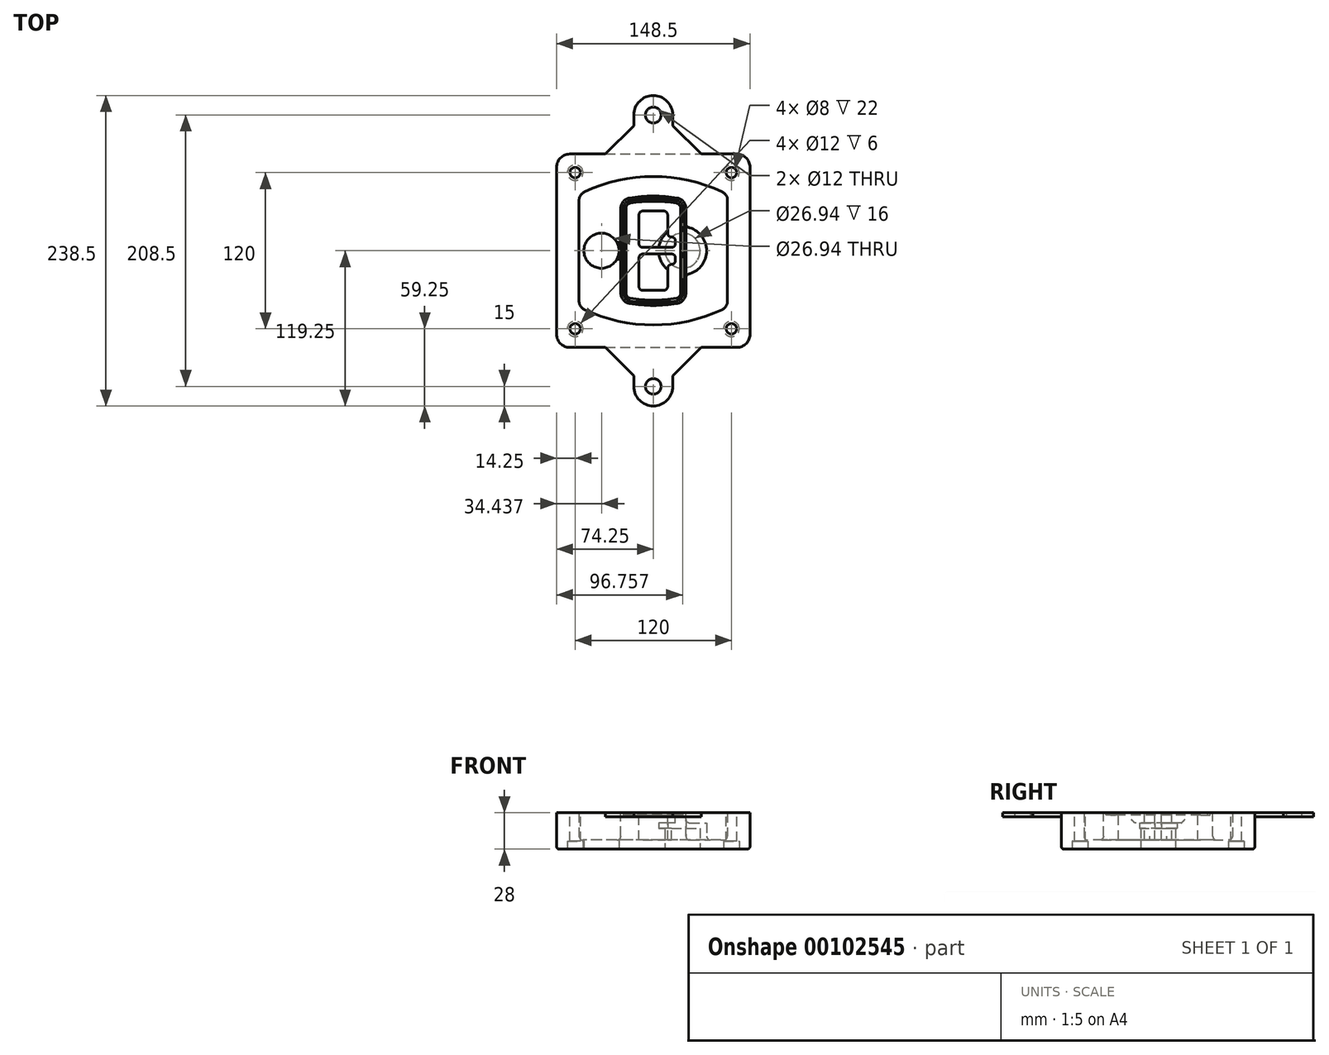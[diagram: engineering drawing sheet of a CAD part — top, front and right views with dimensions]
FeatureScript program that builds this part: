
annotation { "Feature Type Name" : "Feature", "Feature Type Description" : "" }
export const myFeature = defineFeature(function(context is Context, id is Id, definition is map)
    precondition{}
    {
        {
            var Q0;
            Q0=qCreatedBy(makeId("Top.planeOp"),FACE);
            var sketch = newSketch(context, id + "F0", { "sketchPlane" : qUnion([Q0])});
            skPoint(sketch, "E0.rect.middle", {"position": v(0, 0) * mm});
            skLineSegment(sketch, "E1.bottom", {"start": v(-64.25, -74.25) * mm, "end": v(64.25, -74.25) * mm});
            skLineSegment(sketch, "E1.top", {"start": v(-64.25, 74.25) * mm, "end": v(64.25, 74.25) * mm});
            skLineSegment(sketch, "E1.left", {"start": v(-74.25, -64.25) * mm, "end": v(-74.25, 64.25) * mm});
            skLineSegment(sketch, "E1.right", {"start": v(74.25, -64.25) * mm, "end": v(74.25, 64.25) * mm});
            skLineSegment(sketch, "E2", {"start": v(-74.25, 74.25) * mm, "end": v(74.25, -74.25) * mm, "construction": true});
            skLineSegment(sketch, "E3", {"start": v(74.25, 74.25) * mm, "end": v(-74.25, -74.25) * mm, "construction": true});
            skCircle(sketch, "E4", {"center": v(-60, 60) * mm, "radius": 4 * mm});
            skCircle(sketch, "E5", {"center": v(60, 60) * mm, "radius": 4 * mm});
            skCircle(sketch, "E6", {"center": v(60, -60) * mm, "radius": 4 * mm});
            skCircle(sketch, "E7", {"center": v(-60, -60) * mm, "radius": 4 * mm});
            skLineSegment(sketch, "E8", {"start": v(-60, 60) * mm, "end": v(60, 60) * mm, "construction": true});
            skLineSegment(sketch, "E9", {"start": v(60, 60) * mm, "end": v(60, -60) * mm, "construction": true});
            skLineSegment(sketch, "E10", {"start": v(60, -60) * mm, "end": v(-60, -60) * mm, "construction": true});
            skLineSegment(sketch, "E11", {"start": v(-60, -60) * mm, "end": v(-60, 60) * mm, "construction": true});
            skLineSegment(sketch, "E12", {"start": v(-60, 38.83) * mm, "end": v(-60, -38.83) * mm});
            skLineSegment(sketch, "E13", {"start": v(60, 38.83) * mm, "end": v(60, -38.83) * mm});
            skArc(sketch, "E14", {"start": v(54.26, 47.88) * mm, "mid": v(0, 60) * mm, "end": v(-54.26, 47.88) * mm});
            skArc(sketch, "E15", {"start": v(-54.26, -47.88) * mm, "mid": v(0, -60) * mm, "end": v(54.26, -47.88) * mm});
            skLineSegment(sketch, "E16", {"start": v(-60, 0) * mm, "end": v(60, 0) * mm, "construction": true});
            skPoint(sketch, "E17.visualSharp", {"position": v(-60, -45) * mm});
            skArc(sketch, "E17.filletArc", {"start": v(-60, -38.83) * mm, "mid": v(-58.44, -44.2) * mm, "end": v(-54.26, -47.88) * mm});
            skPoint(sketch, "E18.visualSharp", {"position": v(-60, 45) * mm});
            skArc(sketch, "E18.filletArc", {"start": v(-54.26, 47.88) * mm, "mid": v(-58.44, 44.2) * mm, "end": v(-60, 38.83) * mm});
            skPoint(sketch, "E19.visualSharp", {"position": v(60, 45) * mm});
            skArc(sketch, "E19.filletArc", {"start": v(60, 38.83) * mm, "mid": v(58.44, 44.2) * mm, "end": v(54.26, 47.88) * mm});
            skPoint(sketch, "E20.visualSharp", {"position": v(60, -45) * mm});
            skArc(sketch, "E20.filletArc", {"start": v(54.26, -47.88) * mm, "mid": v(58.44, -44.2) * mm, "end": v(60, -38.83) * mm});
            skPoint(sketch, "E21.visualSharp", {"position": v(-74.25, 74.25) * mm});
            skArc(sketch, "E21.filletArc", {"start": v(-64.25, 74.25) * mm, "mid": v(-71.32, 71.32) * mm, "end": v(-74.25, 64.25) * mm});
            skPoint(sketch, "E22.visualSharp", {"position": v(74.25, 74.25) * mm});
            skArc(sketch, "E22.filletArc", {"start": v(74.25, 64.25) * mm, "mid": v(71.32, 71.32) * mm, "end": v(64.25, 74.25) * mm});
            skPoint(sketch, "E23.visualSharp", {"position": v(74.25, -74.25) * mm});
            skArc(sketch, "E23.filletArc", {"start": v(64.25, -74.25) * mm, "mid": v(71.32, -71.32) * mm, "end": v(74.25, -64.25) * mm});
            skPoint(sketch, "E24.visualSharp", {"position": v(-74.25, -74.25) * mm});
            skArc(sketch, "E24.filletArc", {"start": v(-74.25, -64.25) * mm, "mid": v(-71.32, -71.32) * mm, "end": v(-64.25, -74.25) * mm});
            skArc(sketch, "E25.0", {"start": v(57, 38.83) * mm, "mid": v(55.9, 42.58) * mm, "end": v(52.98, 45.17) * mm});
            skLineSegment(sketch, "E25.1", {"start": v(57, 38.83) * mm, "end": v(57, -38.83) * mm});
            skArc(sketch, "E25.2", {"start": v(52.98, -45.17) * mm, "mid": v(55.9, -42.58) * mm, "end": v(57, -38.83) * mm});
            skArc(sketch, "E25.3", {"start": v(-52.98, -45.17) * mm, "mid": v(0, -57) * mm, "end": v(52.98, -45.17) * mm});
            skArc(sketch, "E25.4", {"start": v(-57, -38.83) * mm, "mid": v(-55.9, -42.58) * mm, "end": v(-52.98, -45.17) * mm});
            skArc(sketch, "E25.5", {"start": v(52.98, 45.17) * mm, "mid": v(0, 57) * mm, "end": v(-52.98, 45.17) * mm});
            skLineSegment(sketch, "E25.6", {"start": v(-57, 38.83) * mm, "end": v(-57, -38.83) * mm});
            skArc(sketch, "E25.7", {"start": v(-52.98, 45.17) * mm, "mid": v(-55.9, 42.58) * mm, "end": v(-57, 38.83) * mm});
            skArc(sketch, "E26.0", {"start": v(-55.96, 51.5) * mm, "mid": v(-61.82, 46.33) * mm, "end": v(-64, 38.83) * mm});
            skArc(sketch, "E26.1", {"start": v(55.96, 51.5) * mm, "mid": v(0, 64) * mm, "end": v(-55.96, 51.5) * mm});
            skArc(sketch, "E26.2", {"start": v(64, 38.83) * mm, "mid": v(61.82, 46.33) * mm, "end": v(55.96, 51.5) * mm});
            skLineSegment(sketch, "E26.3", {"start": v(64, 38.83) * mm, "end": v(64, -38.83) * mm});
            skArc(sketch, "E26.4", {"start": v(55.96, -51.5) * mm, "mid": v(61.82, -46.33) * mm, "end": v(64, -38.83) * mm});
            skLineSegment(sketch, "E26.5", {"start": v(-64, 38.83) * mm, "end": v(-64, -38.83) * mm});
            skArc(sketch, "E26.6", {"start": v(-55.96, -51.5) * mm, "mid": v(0, -64) * mm, "end": v(55.96, -51.5) * mm});
            skArc(sketch, "E26.7", {"start": v(-64, -38.83) * mm, "mid": v(-61.82, -46.33) * mm, "end": v(-55.96, -51.5) * mm});
            skSolve(sketch);
        }
        {
            var Q0;
            Q0=makeQuery(id+"F0.imprint","IMPRINT",FACE,{"disambiguationData":[TD([[makeQuery(id+"F0.imprint","IMPRINT",EDGE,{"derivedFrom":sQuery(id+"F0.wireOp",EDGE,"E1.bottom")}),1.0]])]});
            var Q1;
            Q1=makeQuery(id+"F0.imprint","IMPRINT",FACE,{"disambiguationData":[TD([[makeQuery(id+"F0.imprint","IMPRINT",EDGE,{"derivedFrom":sQuery(id+"F0.wireOp",EDGE,"E12")}),1.0]])]});
            var Q2;
            Q2=makeQuery(id+"F0.imprint","IMPRINT",FACE,{"disambiguationData":[TD([[makeQuery(id+"F0.imprint","IMPRINT",EDGE,{"derivedFrom":sQuery(id+"F0.wireOp",EDGE,"E25.0")}),1.0]])]});
            var Q3;
            Q3=makeQuery(id+"F0.imprint","IMPRINT",FACE,{"disambiguationData":[TD([[makeQuery(id+"F0.imprint","IMPRINT",EDGE,{"derivedFrom":sQuery(id+"F0.wireOp",EDGE,"E12")}),-1.0]])]});
            extrude(context, id + "F1", {"entities" : qUnion([Q0, Q1, Q2, Q3]), "oppositeDirection" : true, "depth" : 25 * mm});
        }
        {
            var Q0;
            Q0=makeQuery(id+"F0.imprint","IMPRINT",FACE,{"disambiguationData":[TD([[makeQuery(id+"F0.imprint","IMPRINT",EDGE,{"derivedFrom":sQuery(id+"F0.wireOp",EDGE,"E12")}),1.0]])]});
            extrude(context, id + "F2", {"entities" : qUnion([Q0]), "operationType" : NewBodyOperationType.ADD, "depth" : 3 * mm});
        }
        {
            var Q0;
            Q0=makeQuery(id+"F0.imprint","IMPRINT",FACE,{"disambiguationData":[TD([[makeQuery(id+"F0.imprint","IMPRINT",EDGE,{"derivedFrom":sQuery(id+"F0.wireOp",EDGE,"E25.0")}),1.0]])]});
            extrude(context, id + "F3", {"entities" : qUnion([Q0]), "operationType" : NewBodyOperationType.REMOVE, "oppositeDirection" : true, "depth" : 18 * mm});
        }
        {
            var Q0;
            Q0=makeQuery(id+"F2.opExtrude","CAP_FACE",FACE,{"disambiguationData":[OSD([sQuery(id+"F0.wireOp",EDGE,"E12"),sQuery(id+"F0.wireOp",EDGE,"E13"),sQuery(id+"F0.wireOp",EDGE,"E14"),sQuery(id+"F0.wireOp",EDGE,"E15"),sQuery(id+"F0.wireOp",EDGE,"E17.filletArc"),sQuery(id+"F0.wireOp",EDGE,"E18.filletArc"),sQuery(id+"F0.wireOp",EDGE,"E19.filletArc"),sQuery(id+"F0.wireOp",EDGE,"E20.filletArc"),sQuery(id+"F0.wireOp",EDGE,"E25.0"),sQuery(id+"F0.wireOp",EDGE,"E25.1"),sQuery(id+"F0.wireOp",EDGE,"E25.2"),sQuery(id+"F0.wireOp",EDGE,"E25.3"),sQuery(id+"F0.wireOp",EDGE,"E25.4"),sQuery(id+"F0.wireOp",EDGE,"E25.5"),sQuery(id+"F0.wireOp",EDGE,"E25.6"),sQuery(id+"F0.wireOp",EDGE,"E25.7")])],"isStart":false});
            var sketch = newSketch(context, id + "F4", { "sketchPlane" : qUnion([Q0])});
            skArc(sketch, "E27.0", {"start": v(-18.34, -40.45) * mm, "mid": v(0, -42) * mm, "end": v(18.34, -40.45) * mm});
            skArc(sketch, "E28.0", {"start": v(18.34, 40.45) * mm, "mid": v(0, 42) * mm, "end": v(-18.34, 40.45) * mm});
            skLineSegment(sketch, "E29", {"start": v(-25, 32.57) * mm, "end": v(-25, -32.57) * mm});
            skLineSegment(sketch, "E30", {"start": v(25, 32.57) * mm, "end": v(25, -32.57) * mm});
            skLineSegment(sketch, "E31", {"start": v(-25, 39.1) * mm, "end": v(25, 39.1) * mm, "construction": true});
            skLineSegment(sketch, "E32", {"start": v(-25, -39.1) * mm, "end": v(25, -39.1) * mm, "construction": true});
            skPoint(sketch, "E33.visualSharp", {"position": v(-25, 39.1) * mm});
            skArc(sketch, "E33.filletArc", {"start": v(-18.34, 40.45) * mm, "mid": v(-23.11, 37.73) * mm, "end": v(-25, 32.57) * mm});
            skPoint(sketch, "E34.visualSharp", {"position": v(25, 39.1) * mm});
            skArc(sketch, "E34.filletArc", {"start": v(25, 32.57) * mm, "mid": v(23.11, 37.73) * mm, "end": v(18.34, 40.45) * mm});
            skPoint(sketch, "E35.visualSharp", {"position": v(25, -39.1) * mm});
            skArc(sketch, "E35.filletArc", {"start": v(18.34, -40.45) * mm, "mid": v(23.11, -37.73) * mm, "end": v(25, -32.57) * mm});
            skPoint(sketch, "E36.visualSharp", {"position": v(-25, -39.1) * mm});
            skArc(sketch, "E36.filletArc", {"start": v(-25, -32.57) * mm, "mid": v(-23.11, -37.73) * mm, "end": v(-18.34, -40.45) * mm});
            skArc(sketch, "E37.0", {"start": v(52.98, 45.17) * mm, "mid": v(0, 57) * mm, "end": v(-52.98, 45.17) * mm});
            skArc(sketch, "E37.1", {"start": v(-52.98, 45.17) * mm, "mid": v(-55.9, 42.58) * mm, "end": v(-57, 38.83) * mm});
            skLineSegment(sketch, "E37.2", {"start": v(-57, 38.83) * mm, "end": v(-57, -38.83) * mm});
            skArc(sketch, "E37.3", {"start": v(-57, -38.83) * mm, "mid": v(-55.9, -42.58) * mm, "end": v(-52.98, -45.17) * mm});
            skArc(sketch, "E37.4", {"start": v(-52.98, -45.17) * mm, "mid": v(0, -57) * mm, "end": v(52.98, -45.17) * mm});
            skArc(sketch, "E37.5", {"start": v(52.98, -45.17) * mm, "mid": v(55.9, -42.58) * mm, "end": v(57, -38.83) * mm});
            skLineSegment(sketch, "E37.6", {"start": v(57, 38.83) * mm, "end": v(57, -38.83) * mm});
            skArc(sketch, "E37.7", {"start": v(57, 38.83) * mm, "mid": v(55.9, 42.58) * mm, "end": v(52.98, 45.17) * mm});
            skLineSegment(sketch, "E38.0", {"start": v(23, 32.57) * mm, "end": v(23, -32.57) * mm});
            skArc(sketch, "E38.1", {"start": v(18, -38.48) * mm, "mid": v(21.58, -36.44) * mm, "end": v(23, -32.57) * mm});
            skArc(sketch, "E38.2", {"start": v(-18, -38.48) * mm, "mid": v(0, -40) * mm, "end": v(18, -38.48) * mm});
            skArc(sketch, "E38.3", {"start": v(-23, -32.57) * mm, "mid": v(-21.58, -36.44) * mm, "end": v(-18, -38.48) * mm});
            skLineSegment(sketch, "E38.4", {"start": v(-23, 32.57) * mm, "end": v(-23, -32.57) * mm});
            skArc(sketch, "E38.5", {"start": v(23, 32.57) * mm, "mid": v(21.58, 36.44) * mm, "end": v(18, 38.48) * mm});
            skArc(sketch, "E38.6", {"start": v(-18, 38.48) * mm, "mid": v(-21.58, 36.44) * mm, "end": v(-23, 32.57) * mm});
            skArc(sketch, "E38.7", {"start": v(18, 38.48) * mm, "mid": v(0, 40) * mm, "end": v(-18, 38.48) * mm});
            skArc(sketch, "E39.0", {"start": v(21, 32.57) * mm, "mid": v(20.06, 35.15) * mm, "end": v(17.67, 36.5) * mm});
            skLineSegment(sketch, "E39.1", {"start": v(21, 32.57) * mm, "end": v(21, -32.57) * mm});
            skArc(sketch, "E39.2", {"start": v(17.67, -36.5) * mm, "mid": v(20.06, -35.15) * mm, "end": v(21, -32.57) * mm});
            skArc(sketch, "E39.3", {"start": v(-17.67, -36.5) * mm, "mid": v(0, -38) * mm, "end": v(17.67, -36.5) * mm});
            skArc(sketch, "E39.4", {"start": v(-21, -32.57) * mm, "mid": v(-20.06, -35.15) * mm, "end": v(-17.67, -36.5) * mm});
            skArc(sketch, "E39.5", {"start": v(17.67, 36.5) * mm, "mid": v(0, 38) * mm, "end": v(-17.67, 36.5) * mm});
            skLineSegment(sketch, "E39.6", {"start": v(-21, 32.57) * mm, "end": v(-21, -32.57) * mm});
            skArc(sketch, "E39.7", {"start": v(-17.67, 36.5) * mm, "mid": v(-20.06, 35.15) * mm, "end": v(-21, 32.57) * mm});
            skLineSegment(sketch, "E40", {"start": v(-25, 0) * mm, "end": v(25, 0) * mm, "construction": true});
            skLineSegment(sketch, "E41", {"start": v(-11, 5.5) * mm, "end": v(-11, 27.5) * mm});
            skLineSegment(sketch, "E42", {"start": v(-8, 30.5) * mm, "end": v(8, 30.5) * mm});
            skLineSegment(sketch, "E43", {"start": v(11, 27.5) * mm, "end": v(11, 13.5) * mm});
            skLineSegment(sketch, "E44", {"start": v(14, 10.5) * mm, "end": v(14, 10.5) * mm});
            skLineSegment(sketch, "E45", {"start": v(17, 7.5) * mm, "end": v(17, 5.5) * mm});
            skLineSegment(sketch, "E46", {"start": v(14, 2.5) * mm, "end": v(-8, 2.5) * mm});
            skPoint(sketch, "E47.visualSharp", {"position": v(-11, 30.5) * mm});
            skArc(sketch, "E47.filletArc", {"start": v(-8, 30.5) * mm, "mid": v(-10.12, 29.62) * mm, "end": v(-11, 27.5) * mm});
            skPoint(sketch, "E48.visualSharp", {"position": v(11, 30.5) * mm});
            skArc(sketch, "E48.filletArc", {"start": v(11, 27.5) * mm, "mid": v(10.12, 29.62) * mm, "end": v(8, 30.5) * mm});
            skPoint(sketch, "E49.visualSharp", {"position": v(11, 10.5) * mm});
            skArc(sketch, "E49.filletArc", {"start": v(11, 13.5) * mm, "mid": v(11.88, 11.38) * mm, "end": v(14, 10.5) * mm});
            skPoint(sketch, "E50.visualSharp", {"position": v(17, 10.5) * mm});
            skArc(sketch, "E50.filletArc", {"start": v(17, 7.5) * mm, "mid": v(16.12, 9.62) * mm, "end": v(14, 10.5) * mm});
            skPoint(sketch, "E51.visualSharp", {"position": v(17, 2.5) * mm});
            skArc(sketch, "E51.filletArc", {"start": v(14, 2.5) * mm, "mid": v(16.12, 3.38) * mm, "end": v(17, 5.5) * mm});
            skPoint(sketch, "E52.visualSharp", {"position": v(-11, 2.5) * mm});
            skArc(sketch, "E52.filletArc", {"start": v(-11, 5.5) * mm, "mid": v(-10.12, 3.38) * mm, "end": v(-8, 2.5) * mm});
            skLineSegment(sketch, "E53.0.MirrorCS", {"start": v(14, -2.5) * mm, "end": v(-8, -2.5) * mm});
            skArc(sketch, "E54.0.MirrorCS", {"start": v(-11, -5.5) * mm, "mid": v(-10.12, -3.38) * mm, "end": v(-8, -2.5) * mm});
            skLineSegment(sketch, "E55.0.MirrorCS", {"start": v(-11, -5.5) * mm, "end": v(-11, -27.5) * mm});
            skArc(sketch, "E56.0.MirrorCS", {"start": v(-8, -30.5) * mm, "mid": v(-10.12, -29.62) * mm, "end": v(-11, -27.5) * mm});
            skLineSegment(sketch, "E57.0.MirrorCS", {"start": v(-8, -30.5) * mm, "end": v(8, -30.5) * mm});
            skArc(sketch, "E58.0.MirrorCS", {"start": v(11, -27.5) * mm, "mid": v(10.12, -29.62) * mm, "end": v(8, -30.5) * mm});
            skLineSegment(sketch, "E59.0.MirrorCS", {"start": v(11, -27.5) * mm, "end": v(11, -13.5) * mm});
            skArc(sketch, "E60.0.MirrorCS", {"start": v(11, -13.5) * mm, "mid": v(11.88, -11.38) * mm, "end": v(14, -10.5) * mm});
            skArc(sketch, "E61.0.MirrorCS", {"start": v(17, -7.5) * mm, "mid": v(16.12, -9.62) * mm, "end": v(14, -10.5) * mm});
            skLineSegment(sketch, "E62.0.MirrorCS", {"start": v(17, -7.5) * mm, "end": v(17, -5.5) * mm});
            skArc(sketch, "E63.0.MirrorCS", {"start": v(14, -2.5) * mm, "mid": v(16.12, -3.38) * mm, "end": v(17, -5.5) * mm});
            skSolve(sketch);
        }
        {
            var Q0;
            Q0=makeQuery(id+"F4.imprint","IMPRINT",FACE,{"disambiguationData":[TD([[makeQuery(id+"F4.imprint","IMPRINT",EDGE,{"derivedFrom":sQuery(id+"F4.wireOp",EDGE,"E27.0")}),1.0]])]});
            var Q1;
            Q1=makeQuery(id+"F4.imprint","IMPRINT",FACE,{"disambiguationData":[TD([[makeQuery(id+"F4.imprint","IMPRINT",EDGE,{"derivedFrom":sQuery(id+"F4.wireOp",EDGE,"E38.0")}),-1.0]])]});
            var Q2;
            Q2=makeQuery(id+"F4.imprint","IMPRINT",FACE,{"disambiguationData":[TD([[makeQuery(id+"F4.imprint","IMPRINT",EDGE,{"derivedFrom":sQuery(id+"F4.wireOp",EDGE,"E39.0")}),1.0]])]});
            extrude(context, id + "F5", {"entities" : qUnion([Q0, Q1, Q2]), "operationType" : NewBodyOperationType.ADD, "endBound" : BoundingType.UP_TO_NEXT, "oppositeDirection" : true, "depth" : 25 * mm});
        }
        {
            var Q0;
            Q0=makeQuery(id+"F4.imprint","IMPRINT",FACE,{"disambiguationData":[TD([[makeQuery(id+"F4.imprint","IMPRINT",EDGE,{"derivedFrom":sQuery(id+"F4.wireOp",EDGE,"E38.0")}),-1.0]])]});
            extrude(context, id + "F6", {"entities" : qUnion([Q0]), "operationType" : NewBodyOperationType.REMOVE, "oppositeDirection" : true, "depth" : 2 * mm});
        }
        {
            var Q0;
            Q0=makeQuery(id+"F1.opExtrude","CAP_FACE",FACE,{"disambiguationData":[OSD([sQuery(id+"F0.wireOp",EDGE,"E1.bottom"),sQuery(id+"F0.wireOp",EDGE,"E1.top"),sQuery(id+"F0.wireOp",EDGE,"E1.left"),sQuery(id+"F0.wireOp",EDGE,"E1.right"),sQuery(id+"F0.wireOp",EDGE,"E4"),sQuery(id+"F0.wireOp",EDGE,"E5"),sQuery(id+"F0.wireOp",EDGE,"E6"),sQuery(id+"F0.wireOp",EDGE,"E7"),sQuery(id+"F0.wireOp",EDGE,"E21.filletArc"),sQuery(id+"F0.wireOp",EDGE,"E22.filletArc"),sQuery(id+"F0.wireOp",EDGE,"E23.filletArc"),sQuery(id+"F0.wireOp",EDGE,"E24.filletArc")])],"isStart":false});
            var sketch = newSketch(context, id + "F7", { "sketchPlane" : qUnion([Q0])});
            skCircle(sketch, "E64", {"center": v(22.5, 0) * mm, "radius": 13.47 * mm});
            skCircle(sketch, "E65", {"center": v(-39.81, 0) * mm, "radius": 13.47 * mm});
            skLineSegment(sketch, "E66", {"start": v(74.25, 0) * mm, "end": v(-74.25, 0) * mm});
            skCircle(sketch, "E67", {"center": v(22.5, 0) * mm, "radius": 18.47 * mm});
            skCircle(sketch, "E68", {"center": v(60, -60) * mm, "radius": 6 * mm});
            skCircle(sketch, "E69", {"center": v(-60, -60) * mm, "radius": 6 * mm});
            skCircle(sketch, "E70", {"center": v(-60, 60) * mm, "radius": 6 * mm});
            skCircle(sketch, "E71", {"center": v(60, 60) * mm, "radius": 6 * mm});
            skSolve(sketch);
        }
        {
            var Q0;
            {var subQ1=sQuery(id+"F7.wireOp",EDGE,"E66");var subQ4=sQuery(id+"F7.wireOp",EDGE,"E64");var subQ6=makeQuery(id+"F7.imprint","INTERSECT",VERTEX,{"disambiguationData":[OD(0.0)],"derivedFrom":[subQ4,subQ1]});Q0=makeQuery(id+"F7.imprint","IMPRINT",FACE,{"disambiguationData":[TD([[makeQuery(id+"F7.imprint","IMPRINT",EDGE,{"disambiguationData":[TD([[subQ6,-1.0]])],"derivedFrom":subQ4}),-1.0]])]});}
            var Q1;
            {var subQ0=sQuery(id+"F7.wireOp",EDGE,"E66");var subQ1=sQuery(id+"F7.wireOp",EDGE,"E64");var subQ3=makeQuery(id+"F7.imprint","INTERSECT",VERTEX,{"disambiguationData":[OD(0.0)],"derivedFrom":[subQ1,subQ0]});Q1=makeQuery(id+"F7.imprint","IMPRINT",FACE,{"disambiguationData":[TD([[makeQuery(id+"F7.imprint","IMPRINT",EDGE,{"disambiguationData":[TD([[subQ3,-1.0]])],"derivedFrom":subQ1}),1.0]])]});}
            var Q2;
            {var subQ0=sQuery(id+"F7.wireOp",EDGE,"E66");var subQ1=sQuery(id+"F7.wireOp",EDGE,"E64");var subQ3=makeQuery(id+"F7.imprint","INTERSECT",VERTEX,{"disambiguationData":[OD(0.0)],"derivedFrom":[subQ1,subQ0]});Q2=makeQuery(id+"F7.imprint","IMPRINT",FACE,{"disambiguationData":[TD([[makeQuery(id+"F7.imprint","IMPRINT",EDGE,{"disambiguationData":[TD([[subQ3,1.0]])],"derivedFrom":subQ1}),1.0]])]});}
            var Q3;
            {var subQ1=sQuery(id+"F7.wireOp",EDGE,"E66");var subQ4=sQuery(id+"F7.wireOp",EDGE,"E64");var subQ6=makeQuery(id+"F7.imprint","INTERSECT",VERTEX,{"disambiguationData":[OD(0.0)],"derivedFrom":[subQ4,subQ1]});Q3=makeQuery(id+"F7.imprint","IMPRINT",FACE,{"disambiguationData":[TD([[makeQuery(id+"F7.imprint","IMPRINT",EDGE,{"disambiguationData":[TD([[subQ6,1.0]])],"derivedFrom":subQ4}),-1.0]])]});}
            extrude(context, id + "F8", {"entities" : qUnion([Q0, Q1, Q2, Q3]), "operationType" : NewBodyOperationType.ADD, "oppositeDirection" : true, "depth" : 20 * mm});
        }
        {
            var Q0;
            {var subQ0=sQuery(id+"F7.wireOp",EDGE,"E66");var subQ1=sQuery(id+"F7.wireOp",EDGE,"E64");var subQ3=makeQuery(id+"F7.imprint","INTERSECT",VERTEX,{"disambiguationData":[OD(0.0)],"derivedFrom":[subQ1,subQ0]});Q0=makeQuery(id+"F7.imprint","IMPRINT",FACE,{"disambiguationData":[TD([[makeQuery(id+"F7.imprint","IMPRINT",EDGE,{"disambiguationData":[TD([[subQ3,-1.0]])],"derivedFrom":subQ1}),1.0]])]});}
            var Q1;
            {var subQ0=sQuery(id+"F7.wireOp",EDGE,"E66");var subQ1=sQuery(id+"F7.wireOp",EDGE,"E64");var subQ3=makeQuery(id+"F7.imprint","INTERSECT",VERTEX,{"disambiguationData":[OD(0.0)],"derivedFrom":[subQ1,subQ0]});Q1=makeQuery(id+"F7.imprint","IMPRINT",FACE,{"disambiguationData":[TD([[makeQuery(id+"F7.imprint","IMPRINT",EDGE,{"disambiguationData":[TD([[subQ3,1.0]])],"derivedFrom":subQ1}),1.0]])]});}
            extrude(context, id + "F9", {"entities" : qUnion([Q0, Q1]), "operationType" : NewBodyOperationType.REMOVE, "oppositeDirection" : true, "depth" : 16 * mm});
        }
        {
            var Q0;
            {var subQ0=sQuery(id+"F7.wireOp",EDGE,"E66");var subQ1=sQuery(id+"F7.wireOp",EDGE,"E65");var subQ3=makeQuery(id+"F7.imprint","INTERSECT",VERTEX,{"disambiguationData":[OD(0.0)],"derivedFrom":[subQ1,subQ0]});Q0=makeQuery(id+"F7.imprint","IMPRINT",FACE,{"disambiguationData":[TD([[makeQuery(id+"F7.imprint","IMPRINT",EDGE,{"disambiguationData":[TD([[subQ3,-1.0]])],"derivedFrom":subQ1}),1.0]])]});}
            var Q1;
            {var subQ0=sQuery(id+"F7.wireOp",EDGE,"E66");var subQ1=sQuery(id+"F7.wireOp",EDGE,"E65");var subQ3=makeQuery(id+"F7.imprint","INTERSECT",VERTEX,{"disambiguationData":[OD(0.0)],"derivedFrom":[subQ1,subQ0]});Q1=makeQuery(id+"F7.imprint","IMPRINT",FACE,{"disambiguationData":[TD([[makeQuery(id+"F7.imprint","IMPRINT",EDGE,{"disambiguationData":[TD([[subQ3,1.0]])],"derivedFrom":subQ1}),1.0]])]});}
            extrude(context, id + "F10", {"entities" : qUnion([Q0, Q1]), "operationType" : NewBodyOperationType.REMOVE, "oppositeDirection" : true, "depth" : 25 * mm});
        }
        {
            var Q0;
            Q0=makeQuery(id+"F7.imprint","IMPRINT",FACE,{"disambiguationData":[TD([[makeQuery(id+"F7.imprint","IMPRINT",EDGE,{"derivedFrom":sQuery(id+"F7.wireOp",EDGE,"E68")}),1.0]])]});
            var Q1;
            Q1=makeQuery(id+"F7.imprint","IMPRINT",FACE,{"disambiguationData":[TD([[makeQuery(id+"F7.imprint","IMPRINT",EDGE,{"derivedFrom":makeQuery(id+"F1.opExtrude","CAP_EDGE",EDGE,{"disambiguationData":[OSD([sQuery(id+"F0.wireOp",EDGE,"E5")])],"isStart":false})}),-1.0]])]});
            var Q2;
            Q2=makeQuery(id+"F7.imprint","IMPRINT",FACE,{"disambiguationData":[TD([[makeQuery(id+"F7.imprint","IMPRINT",EDGE,{"derivedFrom":sQuery(id+"F7.wireOp",EDGE,"E69")}),1.0]])]});
            var Q3;
            Q3=makeQuery(id+"F7.imprint","IMPRINT",FACE,{"disambiguationData":[TD([[makeQuery(id+"F7.imprint","IMPRINT",EDGE,{"derivedFrom":makeQuery(id+"F1.opExtrude","CAP_EDGE",EDGE,{"disambiguationData":[OSD([sQuery(id+"F0.wireOp",EDGE,"E4")])],"isStart":false})}),-1.0]])]});
            var Q4;
            Q4=makeQuery(id+"F7.imprint","IMPRINT",FACE,{"disambiguationData":[TD([[makeQuery(id+"F7.imprint","IMPRINT",EDGE,{"derivedFrom":sQuery(id+"F7.wireOp",EDGE,"E70")}),1.0]])]});
            var Q5;
            Q5=makeQuery(id+"F7.imprint","IMPRINT",FACE,{"disambiguationData":[TD([[makeQuery(id+"F7.imprint","IMPRINT",EDGE,{"derivedFrom":makeQuery(id+"F1.opExtrude","CAP_EDGE",EDGE,{"disambiguationData":[OSD([sQuery(id+"F0.wireOp",EDGE,"E7")])],"isStart":false})}),-1.0]])]});
            var Q6;
            Q6=makeQuery(id+"F7.imprint","IMPRINT",FACE,{"disambiguationData":[TD([[makeQuery(id+"F7.imprint","IMPRINT",EDGE,{"derivedFrom":sQuery(id+"F7.wireOp",EDGE,"E71")}),1.0]])]});
            var Q7;
            Q7=makeQuery(id+"F7.imprint","IMPRINT",FACE,{"disambiguationData":[TD([[makeQuery(id+"F7.imprint","IMPRINT",EDGE,{"derivedFrom":makeQuery(id+"F1.opExtrude","CAP_EDGE",EDGE,{"disambiguationData":[OSD([sQuery(id+"F0.wireOp",EDGE,"E6")])],"isStart":false})}),-1.0]])]});
            extrude(context, id + "F11", {"entities" : qUnion([Q0, Q1, Q2, Q3, Q4, Q5, Q6, Q7]), "operationType" : NewBodyOperationType.REMOVE, "oppositeDirection" : true, "depth" : 6 * mm});
        }
        {
            var Q0;
            Q0=makeQuery(id+"F9.boolean.opBoolean","COPY",FACE,{"derivedFrom":makeQuery(id+"F9.opExtrude","CAP_FACE",FACE,{"disambiguationData":[OSD([sQuery(id+"F7.wireOp",EDGE,"E64")])],"isStart":false})});
            var sketch = newSketch(context, id + "F12", { "sketchPlane" : qUnion([Q0])});
            skArc(sketch, "E72.0", {"start": v(11, 14.45) * mm, "mid": v(6.45, 9.13) * mm, "end": v(4.2, 2.5) * mm});
            skArc(sketch, "E72.1", {"start": v(4.2, -2.5) * mm, "mid": v(6.45, -9.13) * mm, "end": v(11, -14.45) * mm});
            skLineSegment(sketch, "E73", {"start": v(4.2, -2.5) * mm, "end": v(14, -2.5) * mm});
            skLineSegment(sketch, "E74.0", {"start": v(14, 2.5) * mm, "end": v(4.2, 2.5) * mm});
            skArc(sketch, "E74.1", {"start": v(14, 2.5) * mm, "mid": v(16.12, 3.38) * mm, "end": v(17, 5.5) * mm});
            skLineSegment(sketch, "E74.2", {"start": v(17, 7.5) * mm, "end": v(17, 5.5) * mm});
            skArc(sketch, "E74.3", {"start": v(17, 7.5) * mm, "mid": v(16.12, 9.62) * mm, "end": v(14, 10.5) * mm});
            skArc(sketch, "E74.4", {"start": v(11, 13.5) * mm, "mid": v(11.88, 11.38) * mm, "end": v(14, 10.5) * mm});
            skLineSegment(sketch, "E74.5", {"start": v(11, 14.45) * mm, "end": v(11, 13.5) * mm});
            skLineSegment(sketch, "E74.7", {"start": v(14, -2.5) * mm, "end": v(4.2, -2.5) * mm});
            skArc(sketch, "E74.8", {"start": v(14, -2.5) * mm, "mid": v(16.12, -3.38) * mm, "end": v(17, -5.5) * mm});
            skLineSegment(sketch, "E74.9", {"start": v(17, -7.5) * mm, "end": v(17, -5.5) * mm});
            skArc(sketch, "E74.10", {"start": v(17, -7.5) * mm, "mid": v(16.12, -9.62) * mm, "end": v(14, -10.5) * mm});
            skArc(sketch, "E74.11", {"start": v(11, -13.5) * mm, "mid": v(11.88, -11.38) * mm, "end": v(14, -10.5) * mm});
            skLineSegment(sketch, "E74.12", {"start": v(11, -14.45) * mm, "end": v(11, -13.5) * mm});
            skPoint(sketch, "E75.orphan", {"position": v(11, -27.5) * mm});
            skPoint(sketch, "E76.orphan", {"position": v(-8, -2.5) * mm});
            skPoint(sketch, "E77.orphan", {"position": v(-8, 2.5) * mm});
            skPoint(sketch, "E78.orphan", {"position": v(11, 27.5) * mm});
            skSolve(sketch);
        }
        {
            var Q0;
            {var subQ7=sQuery(id+"F12.wireOp",EDGE,"E72.0");var subQ14=sQuery(id+"F12.wireOp",EDGE,"E72.1");var subQ16=sQuery(id+"F12.wireOp",EDGE,"E74.1");var subQ18=sQuery(id+"F12.wireOp",EDGE,"E74.8");Q0=qUnion([makeQuery(id+"F12.imprint","IMPRINT",FACE,{"disambiguationData":[TD([[makeQuery(id+"F12.imprint","IMPRINT",EDGE,{"derivedFrom":subQ7}),1.0]])]}),makeQuery(id+"F12.imprint","IMPRINT",FACE,{"disambiguationData":[TD([[makeQuery(id+"F12.imprint","IMPRINT",EDGE,{"derivedFrom":subQ14}),1.0]])]}),makeQuery(id+"F12.imprint","IMPRINT",FACE,{"disambiguationData":[TD([[makeQuery(id+"F12.imprint","IMPRINT",EDGE,{"derivedFrom":subQ16}),1.0]])]}),makeQuery(id+"F12.imprint","IMPRINT",FACE,{"disambiguationData":[TD([[makeQuery(id+"F12.imprint","IMPRINT",EDGE,{"derivedFrom":subQ18}),-1.0]])]})]);}
            var Q1;
            Q1=makeQuery(id+"F5.boolean.opBoolean","SPLIT",FACE,{"disambiguationData":[TD([makeQuery(id+"F5.opExtrude","SWEPT_FACE",FACE,{"disambiguationData":[OSD([sQuery(id+"F4.wireOp",EDGE,"E41")])]})])],"derivedFrom":makeQuery(id+"F3.boolean.opBoolean","COPY",FACE,{"derivedFrom":makeQuery(id+"F3.opExtrude","CAP_FACE",FACE,{"disambiguationData":[OSD([sQuery(id+"F0.wireOp",EDGE,"E25.0"),sQuery(id+"F0.wireOp",EDGE,"E25.1"),sQuery(id+"F0.wireOp",EDGE,"E25.2"),sQuery(id+"F0.wireOp",EDGE,"E25.3"),sQuery(id+"F0.wireOp",EDGE,"E25.4"),sQuery(id+"F0.wireOp",EDGE,"E25.5"),sQuery(id+"F0.wireOp",EDGE,"E25.6"),sQuery(id+"F0.wireOp",EDGE,"E25.7")])],"isStart":false})})});
            extrude(context, id + "F13", {"entities" : qUnion([Q0]), "operationType" : NewBodyOperationType.REMOVE, "endBound" : BoundingType.UP_TO_SURFACE, "endBoundEntityFace" : qUnion([Q1]), "depth" : 25 * mm});
        }
        {
            var Q0;
            Q0=makeQuery(id+"F3.boolean.opBoolean","COPY",EDGE,{"derivedFrom":makeQuery(id+"F3.opExtrude","CAP_EDGE",EDGE,{"disambiguationData":[OSD([sQuery(id+"F0.wireOp",EDGE,"E25.6")])],"isStart":false})});
            var Q1;
            Q1=makeQuery(id+"F8.boolean.opBoolean","INTERSECT",EDGE,{"derivedFrom":[makeQuery(id+"F5.opExtrude","SWEPT_FACE",FACE,{"disambiguationData":[OSD([sQuery(id+"F4.wireOp",EDGE,"E30")])]}),makeQuery(id+"F8.opExtrude","CAP_FACE",FACE,{"disambiguationData":[OSD([sQuery(id+"F7.wireOp",EDGE,"E67")])],"isStart":false})]});
            var Q2;
            Q2=makeQuery(id+"F8.boolean.opBoolean","INTERSECT",EDGE,{"disambiguationData":[OD(1.0)],"derivedFrom":[makeQuery(id+"F5.opExtrude","SWEPT_FACE",FACE,{"disambiguationData":[OSD([sQuery(id+"F4.wireOp",EDGE,"E30")])]}),makeQuery(id+"F8.opExtrude","SWEPT_FACE",FACE,{"disambiguationData":[OSD([sQuery(id+"F7.wireOp",EDGE,"E67")])]})]});
            var Q3;
            {var subQ0=sQuery(id+"F4.wireOp",EDGE,"E30");Q3=makeQuery(id+"F8.boolean.opBoolean","SPLIT",EDGE,{"disambiguationData":[TD([makeQuery(id+"F5.opExtrude","SWEPT_FACE",FACE,{"disambiguationData":[OSD([sQuery(id+"F4.wireOp",EDGE,"E35.filletArc")])]})])],"derivedFrom":makeQuery(id+"F5.opExtrude","CAP_EDGE",EDGE,{"disambiguationData":[OSD([subQ0])],"isStart":false})});}
            var Q4;
            {var subQ0=sQuery(id+"F0.wireOp",EDGE,"E25.7");var subQ1=sQuery(id+"F0.wireOp",EDGE,"E25.1");var subQ2=sQuery(id+"F0.wireOp",EDGE,"E25.6");var subQ3=sQuery(id+"F0.wireOp",EDGE,"E25.5");var subQ4=sQuery(id+"F0.wireOp",EDGE,"E25.4");var subQ5=sQuery(id+"F0.wireOp",EDGE,"E25.0");var subQ6=sQuery(id+"F0.wireOp",EDGE,"E25.2");var subQ7=sQuery(id+"F0.wireOp",EDGE,"E25.3");Q4=makeQuery(id+"F8.boolean.opBoolean","INTERSECT",EDGE,{"derivedFrom":[makeQuery(id+"F5.boolean.opBoolean","SPLIT",FACE,{"disambiguationData":[TD([makeQuery(id+"F2.opExtrude","SWEPT_FACE",FACE,{"disambiguationData":[OSD([subQ5])]})])],"derivedFrom":makeQuery(id+"F3.boolean.opBoolean","COPY",FACE,{"derivedFrom":makeQuery(id+"F3.opExtrude","CAP_FACE",FACE,{"disambiguationData":[OSD([subQ5,subQ1,subQ6,subQ7,subQ4,subQ3,subQ2,subQ0])],"isStart":false})})}),makeQuery(id+"F8.opExtrude","SWEPT_FACE",FACE,{"disambiguationData":[OSD([sQuery(id+"F7.wireOp",EDGE,"E67")])]})]});}
            var Q5;
            Q5=makeQuery(id+"F8.boolean.opBoolean","INTERSECT",EDGE,{"disambiguationData":[OD(0.0)],"derivedFrom":[makeQuery(id+"F5.opExtrude","SWEPT_FACE",FACE,{"disambiguationData":[OSD([sQuery(id+"F4.wireOp",EDGE,"E30")])]}),makeQuery(id+"F8.opExtrude","SWEPT_FACE",FACE,{"disambiguationData":[OSD([sQuery(id+"F7.wireOp",EDGE,"E67")])]})]});
            fillet(context, id + "F14", {"entities" : qUnion([Q0, Q1, Q2, Q3, Q4, Q5]), "radius" : 3 * mm, "tangentPropagation" : true, "allowEdgeOverflow" : false});
        }
        {
            var Q0;
            Q0=makeQuery(id+"F1.opExtrude","CAP_EDGE",EDGE,{"disambiguationData":[OSD([sQuery(id+"F0.wireOp",EDGE,"E1.bottom")])],"isStart":false});
            fillet(context, id + "F15", {"entities" : qUnion([Q0]), "radius" : 2 * mm, "tangentPropagation" : true, "allowEdgeOverflow" : false});
        }
        {
            var Q0;
            {var subQ0=sQuery(id+"F0.wireOp",EDGE,"E22.filletArc");var subQ1=sQuery(id+"F0.wireOp",EDGE,"E7");var subQ2=sQuery(id+"F0.wireOp",EDGE,"E6");var subQ3=sQuery(id+"F0.wireOp",EDGE,"E5");var subQ4=sQuery(id+"F0.wireOp",EDGE,"E4");var subQ5=sQuery(id+"F0.wireOp",EDGE,"E1.bottom");var subQ6=sQuery(id+"F0.wireOp",EDGE,"E21.filletArc");var subQ7=sQuery(id+"F0.wireOp",EDGE,"E1.top");var subQ8=sQuery(id+"F0.wireOp",EDGE,"E1.left");var subQ9=sQuery(id+"F0.wireOp",EDGE,"E1.right");var subQ10=sQuery(id+"F0.wireOp",EDGE,"E23.filletArc");var subQ11=sQuery(id+"F0.wireOp",EDGE,"E24.filletArc");Q0=makeQuery(id+"F2.boolean.opBoolean","SPLIT",FACE,{"disambiguationData":[TD([makeQuery(id+"F1.opExtrude","SWEPT_FACE",FACE,{"disambiguationData":[OSD([subQ5])]})])],"derivedFrom":makeQuery(id+"F1.opExtrude","CAP_FACE",FACE,{"disambiguationData":[OSD([subQ5,subQ7,subQ8,subQ9,subQ4,subQ3,subQ2,subQ1,subQ6,subQ0,subQ10,subQ11])],"isStart":true})});}
            var sketch = newSketch(context, id + "F16", { "sketchPlane" : qUnion([Q0])});
            skLineSegment(sketch, "E79", {"start": v(0, 74.25) * mm, "end": v(0, 104.25) * mm, "construction": true});
            skCircle(sketch, "E80", {"center": v(0, 104.25) * mm, "radius": 6 * mm});
            skLineSegment(sketch, "E81", {"start": v(-15, 96.05) * mm, "end": v(-15, 104.25) * mm});
            skArc(sketch, "E82", {"start": v(15, 104.25) * mm, "mid": v(0, 119.25) * mm, "end": v(-15, 104.25) * mm});
            skLineSegment(sketch, "E83", {"start": v(-15, 96.05) * mm, "end": v(-36.8, 74.25) * mm});
            skLineSegment(sketch, "E84", {"start": v(15, 96.05) * mm, "end": v(36.8, 74.25) * mm});
            skLineSegment(sketch, "E85", {"start": v(15, 104.25) * mm, "end": v(15, 96.05) * mm});
            skLineSegment(sketch, "E86", {"start": v(-74.25, 0) * mm, "end": v(74.25, 0) * mm, "construction": true});
            skLineSegment(sketch, "E87.MirrorCS", {"start": v(-15, -96.05) * mm, "end": v(-36.8, -74.25) * mm});
            skLineSegment(sketch, "E88.MirrorCS", {"start": v(-15, -96.05) * mm, "end": v(-15, -104.25) * mm});
            skArc(sketch, "E89.MirrorCS", {"start": v(15, -104.25) * mm, "mid": v(0, -119.25) * mm, "end": v(-15, -104.25) * mm});
            skCircle(sketch, "E90.MirrorC", {"center": v(0, -104.25) * mm, "radius": 6 * mm});
            skLineSegment(sketch, "E91.MirrorCS", {"start": v(15, -104.25) * mm, "end": v(15, -96.05) * mm});
            skLineSegment(sketch, "E92.MirrorCS", {"start": v(15, -96.05) * mm, "end": v(36.8, -74.25) * mm});
            skSolve(sketch);
        }
        {
            var Q0;
            Q0=makeQuery(id+"F16.imprint","IMPRINT",FACE,{"disambiguationData":[TD([[makeQuery(id+"F16.imprint","IMPRINT",EDGE,{"derivedFrom":sQuery(id+"F16.wireOp",EDGE,"E80")}),-1.0]])]});
            var Q1;
            {var subQ0=sQuery(id+"F16.wireOp",EDGE,"E87.MirrorCS");Q1=makeQuery(id+"F16.imprint","IMPRINT",FACE,{"disambiguationData":[TD([[makeQuery(id+"F16.imprint","IMPRINT",EDGE,{"derivedFrom":subQ0}),-1.0]])]});}
            var Q2;
            Q2=makeQuery(id+"F16.imprint","IMPRINT",FACE,{"disambiguationData":[TD([[makeQuery(id+"F16.imprint","IMPRINT",EDGE,{"derivedFrom":makeQuery(id+"F1.opExtrude","CAP_EDGE",EDGE,{"disambiguationData":[OSD([sQuery(id+"F0.wireOp",EDGE,"E1.left")])],"isStart":true})}),-1.0]])]});
            var Q3;
            Q3=makeQuery(id+"F2.opExtrude","CAP_FACE",FACE,{"disambiguationData":[OSD([sQuery(id+"F0.wireOp",EDGE,"E12"),sQuery(id+"F0.wireOp",EDGE,"E13"),sQuery(id+"F0.wireOp",EDGE,"E14"),sQuery(id+"F0.wireOp",EDGE,"E15"),sQuery(id+"F0.wireOp",EDGE,"E17.filletArc"),sQuery(id+"F0.wireOp",EDGE,"E18.filletArc"),sQuery(id+"F0.wireOp",EDGE,"E19.filletArc"),sQuery(id+"F0.wireOp",EDGE,"E20.filletArc"),sQuery(id+"F0.wireOp",EDGE,"E25.0"),sQuery(id+"F0.wireOp",EDGE,"E25.1"),sQuery(id+"F0.wireOp",EDGE,"E25.2"),sQuery(id+"F0.wireOp",EDGE,"E25.3"),sQuery(id+"F0.wireOp",EDGE,"E25.4"),sQuery(id+"F0.wireOp",EDGE,"E25.5"),sQuery(id+"F0.wireOp",EDGE,"E25.6"),sQuery(id+"F0.wireOp",EDGE,"E25.7")])],"isStart":false});
            extrude(context, id + "F17", {"entities" : qUnion([Q0, Q1, Q2]), "operationType" : NewBodyOperationType.ADD, "endBound" : BoundingType.UP_TO_SURFACE, "endBoundEntityFace" : qUnion([Q3]), "depth" : 25 * mm});
        }
    });
